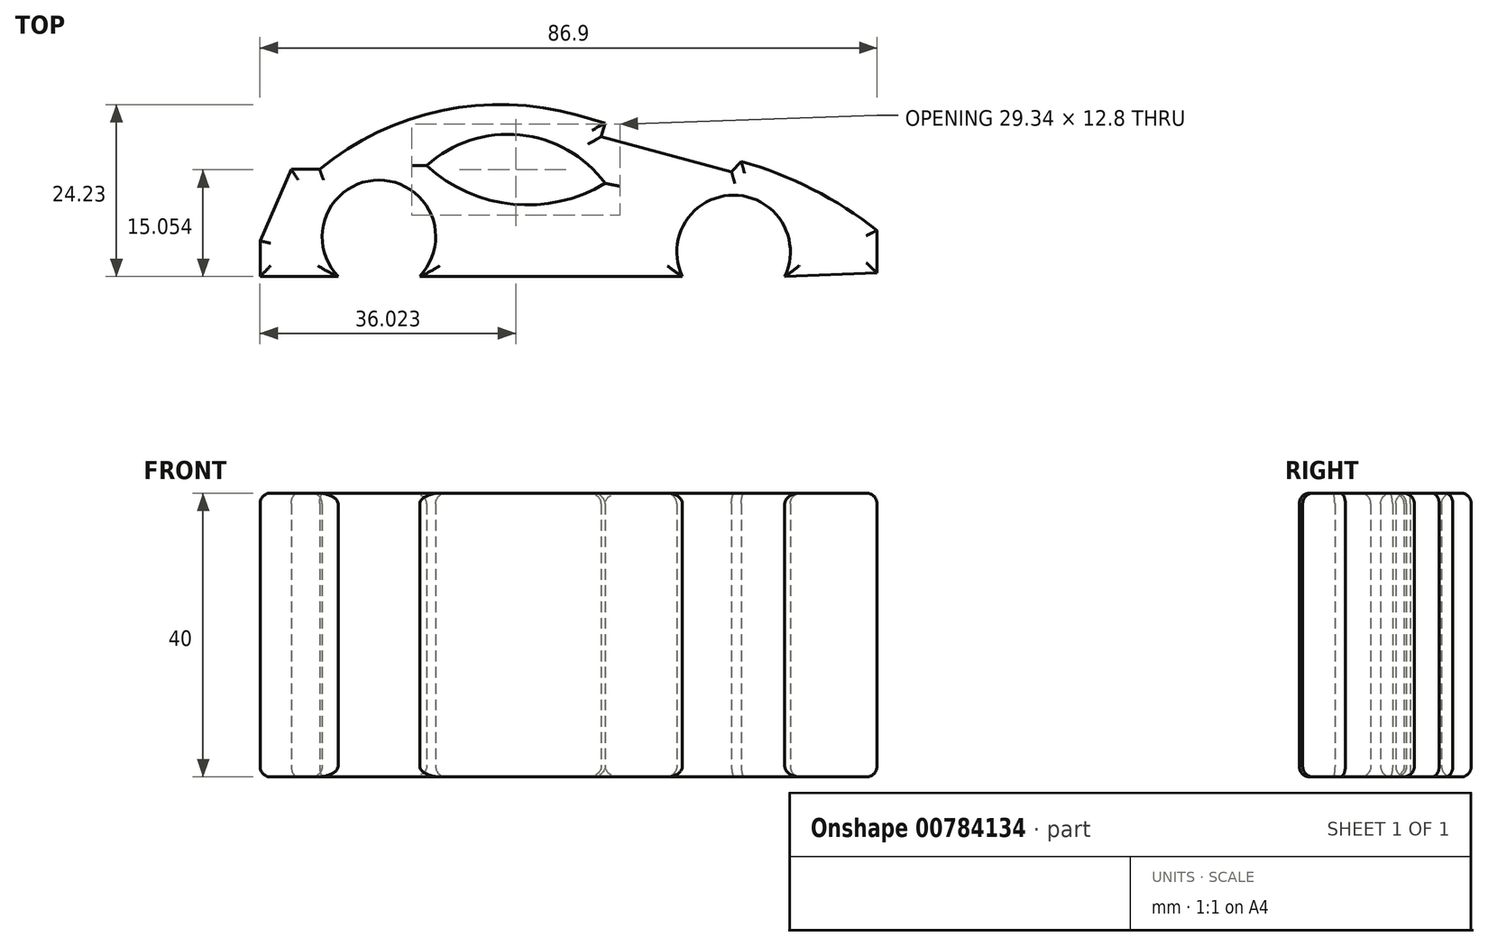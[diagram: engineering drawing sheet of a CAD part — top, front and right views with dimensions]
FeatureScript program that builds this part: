
annotation { "Feature Type Name" : "Feature", "Feature Type Description" : "" }
export const myFeature = defineFeature(function(context is Context, id is Id, definition is map)
    precondition{}
    {
        {
            var Q0;
            Q0=qCreatedBy(makeId("Top.planeOp"),FACE);
            var sketch = newSketch(context, id + "F0", { "sketchPlane" : qUnion([Q0])});
            skPoint(sketch, "E0.endSnap0", {"position": v(-51.7, 68.32) * mm});
            skArc(sketch, "E1", {"start": v(33.87, -6.49) * mm, "mid": v(26.66, 4.97) * mm, "end": v(19.44, -6.49) * mm});
            skArc(sketch, "E2", {"start": v(-17.56, -6.48) * mm, "mid": v(-23.3, 7.1) * mm, "end": v(-29.04, -6.48) * mm});
            skLineSegment(sketch, "E3", {"start": v(-17.56, -6.48) * mm, "end": v(19.44, -6.49) * mm});
            skLineSegment(sketch, "E4", {"start": v(-40.04, -6.48) * mm, "end": v(-29.04, -6.48) * mm});
            skLineSegment(sketch, "E5", {"start": v(-40.04, -1.48) * mm, "end": v(-40.04, -6.48) * mm});
            skLineSegment(sketch, "E6", {"start": v(4.65, 16.24) * mm, "end": v(27.75, 9.73) * mm});
            skArc(sketch, "E7", {"start": v(4.65, 16.24) * mm, "mid": v(-14.44, 16.89) * mm, "end": v(-31.65, 8.6) * mm});
            skLineSegment(sketch, "E8", {"start": v(-40.04, -1.48) * mm, "end": v(-35.65, 8.6) * mm});
            skLineSegment(sketch, "E9", {"start": v(-35.65, 8.6) * mm, "end": v(-31.65, 8.6) * mm});
            skArc(sketch, "E10", {"start": v(46.86, 0) * mm, "mid": v(37.78, 5.8) * mm, "end": v(27.75, 9.73) * mm});
            skLineSegment(sketch, "E11", {"start": v(46.86, 0) * mm, "end": v(46.86, -6) * mm});
            skLineSegment(sketch, "E12", {"start": v(46.86, -6) * mm, "end": v(33.87, -6.49) * mm});
            skArc(sketch, "E13", {"start": v(8.56, 6.65) * mm, "mid": v(-3.44, 13.47) * mm, "end": v(-16.55, 9.13) * mm});
            skArc(sketch, "E14", {"start": v(-16.55, 9.13) * mm, "mid": v(-4.41, 3.7) * mm, "end": v(8.56, 6.65) * mm});
            skLineSegment(sketch, "E15", {"start": v(27.75, 9.73) * mm, "end": v(26.37, 8.28) * mm});
            skLineSegment(sketch, "E16", {"start": v(8.56, 15.14) * mm, "end": v(8.02, 13.21) * mm});
            skLineSegment(sketch, "E17", {"start": v(8.02, 13.21) * mm, "end": v(26.37, 8.28) * mm});
            skSolve(sketch);
        }
        {
            var Q0;
            Q0=makeQuery(id+"F0.imprint","IMPRINT",FACE,{"disambiguationData":[TD([[makeQuery(id+"F0.imprint","IMPRINT",EDGE,{"derivedFrom":sQuery(id+"F0.wireOp",EDGE,"E1")}),-1.0]])]});
            extrude(context, id + "F1", {"entities" : qUnion([Q0]), "depth" : 40 * mm, "offsetDistance" : 25 * mm});
        }
        {
            var Q0;
            Q0=makeQuery(id+"F1.opExtrude","CAP_FACE",FACE,{"disambiguationData":[OSD([sQuery(id+"F0.wireOp",EDGE,"E1"),sQuery(id+"F0.wireOp",EDGE,"E2"),sQuery(id+"F0.wireOp",EDGE,"E3"),sQuery(id+"F0.wireOp",EDGE,"E4"),sQuery(id+"F0.wireOp",EDGE,"E5"),sQuery(id+"F0.wireOp",EDGE,"E6"),sQuery(id+"F0.wireOp",EDGE,"E7"),sQuery(id+"F0.wireOp",EDGE,"E8"),sQuery(id+"F0.wireOp",EDGE,"E9"),sQuery(id+"F0.wireOp",EDGE,"E10"),sQuery(id+"F0.wireOp",EDGE,"E11"),sQuery(id+"F0.wireOp",EDGE,"E12"),sQuery(id+"F0.wireOp",EDGE,"E13"),sQuery(id+"F0.wireOp",EDGE,"E14"),sQuery(id+"F0.wireOp",EDGE,"E15"),sQuery(id+"F0.wireOp",EDGE,"E16"),sQuery(id+"F0.wireOp",EDGE,"E17")])],"isStart":false});
            fillet(context, id + "F2", {"entities" : qUnion([Q0]), "radius" : 1.5 * mm, "tangentPropagation" : true, "allowEdgeOverflow" : false});
        }
        {
            var Q0;
            Q0=makeQuery(id+"F1.opExtrude","CAP_FACE",FACE,{"disambiguationData":[OSD([sQuery(id+"F0.wireOp",EDGE,"E1"),sQuery(id+"F0.wireOp",EDGE,"E2"),sQuery(id+"F0.wireOp",EDGE,"E3"),sQuery(id+"F0.wireOp",EDGE,"E4"),sQuery(id+"F0.wireOp",EDGE,"E5"),sQuery(id+"F0.wireOp",EDGE,"E6"),sQuery(id+"F0.wireOp",EDGE,"E7"),sQuery(id+"F0.wireOp",EDGE,"E8"),sQuery(id+"F0.wireOp",EDGE,"E9"),sQuery(id+"F0.wireOp",EDGE,"E10"),sQuery(id+"F0.wireOp",EDGE,"E11"),sQuery(id+"F0.wireOp",EDGE,"E12"),sQuery(id+"F0.wireOp",EDGE,"E13"),sQuery(id+"F0.wireOp",EDGE,"E14"),sQuery(id+"F0.wireOp",EDGE,"E15"),sQuery(id+"F0.wireOp",EDGE,"E16"),sQuery(id+"F0.wireOp",EDGE,"E17")])],"isStart":true});
            fillet(context, id + "F3", {"entities" : qUnion([Q0]), "radius" : 1.5 * mm, "tangentPropagation" : true, "allowEdgeOverflow" : false});
        }
    });
